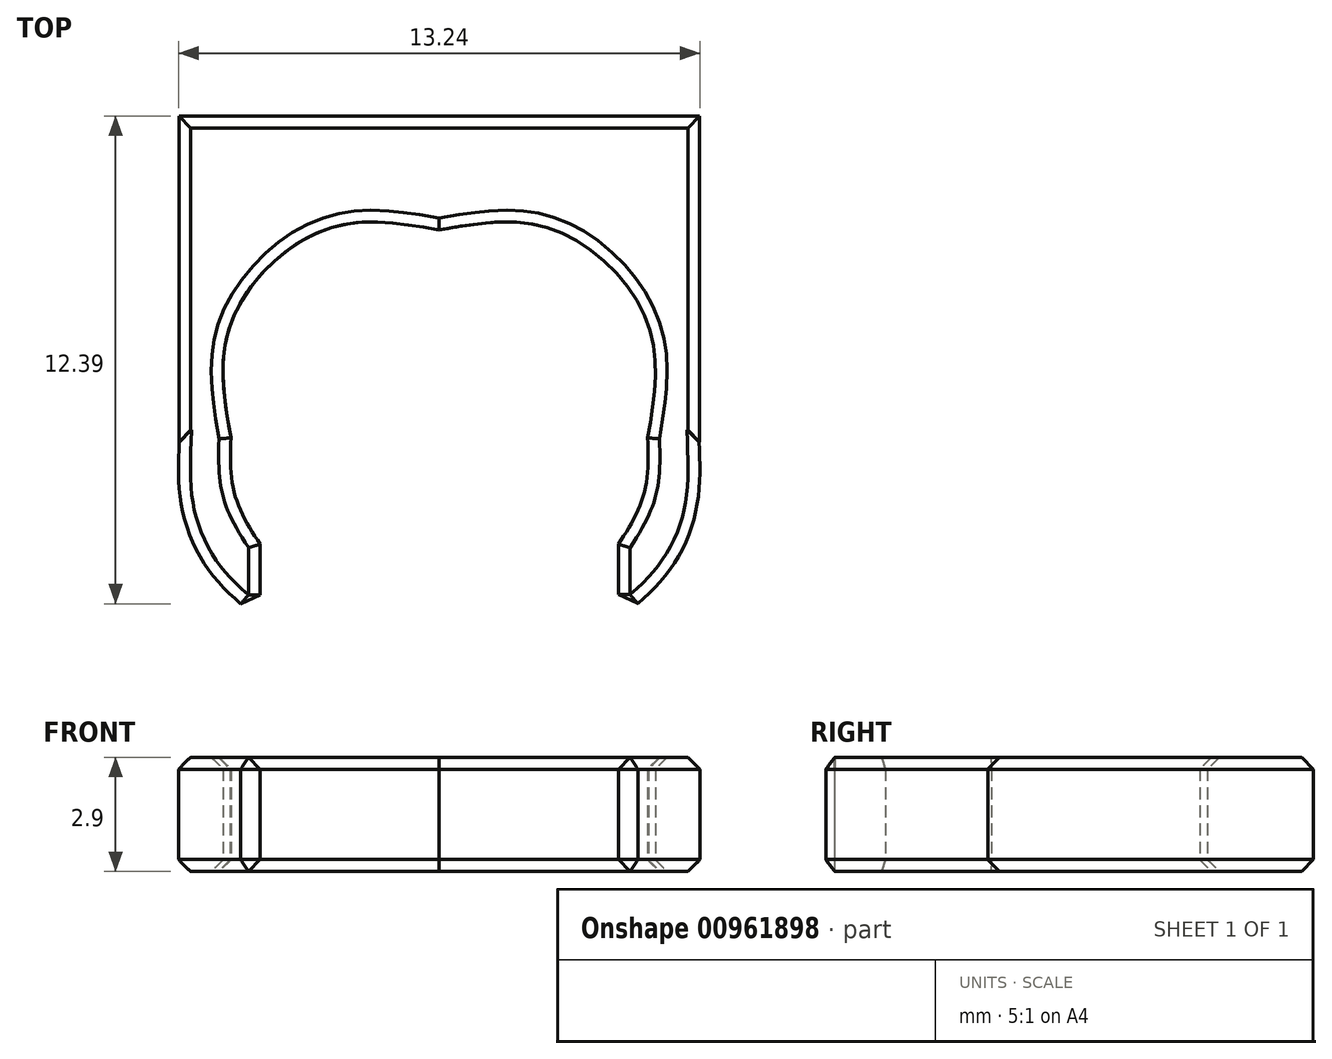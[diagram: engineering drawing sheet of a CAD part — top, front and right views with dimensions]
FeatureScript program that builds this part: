
annotation { "Feature Type Name" : "Feature", "Feature Type Description" : "" }
export const myFeature = defineFeature(function(context is Context, id is Id, definition is map)
    precondition{}
    {
        {
            var Q0;
            Q0=qCreatedBy(makeId("Top.planeOp"),FACE);
            var sketch = newSketch(context, id + "F0", { "sketchPlane" : qUnion([Q0])});
            skLineSegment(sketch, "E0", {"start": v(-6.61, 6.4) * mm, "end": v(-6.61, -1.61) * mm});
            skLineSegment(sketch, "E1", {"start": v(-6.61, -1.61) * mm, "end": v(-6.61, -1.88) * mm});
            skLineSegment(sketch, "E2", {"start": v(4.55, -4.47) * mm, "end": v(4.55, -6.4) * mm});
            skLineSegment(sketch, "E3", {"start": v(6.6, -1.88) * mm, "end": v(6.61, -1.88) * mm});
            skLineSegment(sketch, "E4", {"start": v(6.61, -1.88) * mm, "end": v(6.61, -1.61) * mm});
            skLineSegment(sketch, "E5", {"start": v(6.61, -1.61) * mm, "end": v(6.61, 6.4) * mm});
            skLineSegment(sketch, "E6", {"start": v(6.61, 6.4) * mm, "end": v(-6.61, 6.4) * mm});
            skFitSpline(sketch, "E7", {"points": [v(-6.61, -1.88) * mm, v(-6.61, -1.88) * mm, v(-6.61, -1.88) * mm, v(-6.6, -1.88) * mm, v(-6.6, -1.88) * mm, v(-6.6, -1.88) * mm]});
            skFitSpline(sketch, "E8", {"points": [v(-6.6, -1.88) * mm, v(-6.53, -3.6) * mm, v(-5.8, -5.22) * mm, v(-4.55, -6.4) * mm]});
            skFitSpline(sketch, "E9", {"points": [v(-4.55, -6.4) * mm, v(-4.55, -6.4) * mm, v(-4.55, -6.4) * mm, v(-4.55, -6.3) * mm, v(-4.55, -4.57) * mm, v(-4.55, -4.48) * mm, v(-4.55, -4.48) * mm, v(-4.55, -4.47) * mm]});
            skFitSpline(sketch, "E10", {"points": [v(-4.55, -4.47) * mm, v(-5.03, -3.66) * mm, v(-5.29, -2.73) * mm, v(-5.3, -1.78) * mm]});
            skFitSpline(sketch, "E11", {"points": [v(-5.3, -1.78) * mm, v(-5.3, 1.14) * mm, v(-2.92, 3.5) * mm, v(0, 3.5) * mm]});
            skFitSpline(sketch, "E12", {"points": [v(0, 3.5) * mm, v(2.92, 3.5) * mm, v(5.3, 1.14) * mm, v(5.3, -1.78) * mm]});
            skFitSpline(sketch, "E13", {"points": [v(5.3, -1.78) * mm, v(5.29, -2.73) * mm, v(5.03, -3.66) * mm, v(4.55, -4.47) * mm]});
            skFitSpline(sketch, "E14", {"points": [v(4.55, -6.4) * mm, v(5.8, -5.21) * mm, v(6.53, -3.6) * mm, v(6.6, -1.88) * mm]});
            skSolve(sketch);
        }
        {
            var Q0;
            Q0=makeQuery(id+"F0.imprint","IMPRINT",FACE,{"disambiguationData":[TD([[makeQuery(id+"F0.imprint","IMPRINT",EDGE,{"derivedFrom":sQuery(id+"F0.wireOp",EDGE,"E0")}),1.0]])]});
            extrude(context, id + "F1", {"entities" : qUnion([Q0]), "depth" : 2.9 * mm, "offsetDistance" : 25.4 * mm});
        }
        {
            var Q0;
            Q0=makeQuery(id+"F1.opExtrude","CAP_FACE",FACE,{"disambiguationData":[OSD([sQuery(id+"F0.wireOp",EDGE,"E0"),sQuery(id+"F0.wireOp",EDGE,"E1"),sQuery(id+"F0.wireOp",EDGE,"E2"),sQuery(id+"F0.wireOp",EDGE,"E3"),sQuery(id+"F0.wireOp",EDGE,"E4"),sQuery(id+"F0.wireOp",EDGE,"E5"),sQuery(id+"F0.wireOp",EDGE,"E6"),sQuery(id+"F0.wireOp",EDGE,"E7"),sQuery(id+"F0.wireOp",EDGE,"E8"),sQuery(id+"F0.wireOp",EDGE,"E9"),sQuery(id+"F0.wireOp",EDGE,"E10"),sQuery(id+"F0.wireOp",EDGE,"E11"),sQuery(id+"F0.wireOp",EDGE,"E12"),sQuery(id+"F0.wireOp",EDGE,"E13"),sQuery(id+"F0.wireOp",EDGE,"E14")])],"isStart":false});
            var Q1;
            Q1=makeQuery(id+"F1.opExtrude","SWEPT_EDGE",EDGE,{"disambiguationData":[OSD([sQuery(id+"F0.wireOp",EDGE,"E8"),sQuery(id+"F0.wireOp",EDGE,"E9")])]});
            var Q2;
            Q2=makeQuery(id+"F1.opExtrude","SWEPT_EDGE",EDGE,{"disambiguationData":[OSD([sQuery(id+"F0.wireOp",EDGE,"E2"),sQuery(id+"F0.wireOp",EDGE,"E14")])]});
            var Q3;
            Q3=makeQuery(id+"F1.opExtrude","CAP_FACE",FACE,{"disambiguationData":[OSD([sQuery(id+"F0.wireOp",EDGE,"E0"),sQuery(id+"F0.wireOp",EDGE,"E1"),sQuery(id+"F0.wireOp",EDGE,"E2"),sQuery(id+"F0.wireOp",EDGE,"E3"),sQuery(id+"F0.wireOp",EDGE,"E4"),sQuery(id+"F0.wireOp",EDGE,"E5"),sQuery(id+"F0.wireOp",EDGE,"E6"),sQuery(id+"F0.wireOp",EDGE,"E7"),sQuery(id+"F0.wireOp",EDGE,"E8"),sQuery(id+"F0.wireOp",EDGE,"E9"),sQuery(id+"F0.wireOp",EDGE,"E10"),sQuery(id+"F0.wireOp",EDGE,"E11"),sQuery(id+"F0.wireOp",EDGE,"E12"),sQuery(id+"F0.wireOp",EDGE,"E13"),sQuery(id+"F0.wireOp",EDGE,"E14")])],"isStart":true});
            chamfer(context, id + "F2", {"entities" : qUnion([Q0, Q1, Q2, Q3]), "width" : 0.3 * mm, "tangentPropagation" : true});
        }
    });
